# Revit family: Führungsklammer-Set, Typ B (I-III)
name_source: partatom
category: HLS-Bauteile
revit_build: Autodesk Revit 2018 (Build: 20190510_1515(x64)
units: mm (PartAtom-declared; Revit-internal decimal feet)

## family parameters
Arbeitsebenenbasiert = Ja
Beim Laden mit Abzugskörper schneiden = Nein
Bemaßung runder Anschluss = Durchmesser verwenden
Gemeinsam genutzt = Ja
Immer vertikal = Nein
Raumberechnungspunkt = Nein
Teiletyp = Normal

## types (3) — shared parameters
Fabrikat = MEFA
Firma = MEFA Befestigungs- und Montagesysteme GmbH
Material = Stahl
Materialname = S235
Mengeneinheit = St
Oberflaeche = feuerstückverzinkt
Vorgabe-Ansicht = 1219 mm
max. zul. Schublast = 4.00 kN
vpe = 1 St

## per-type parameters (varying)
| type | Artikelnummer | Faktor1 | Gewicht | Gewicht pro Bauteil | Gewindestangentyp | Klemmweite | Klemmweite Flansch max. | Klemmweite Flansch min. | Kurztext1 | Kurztext2 | Typ | min. Klemmdicke |
| Loslager ohne Abhebesicherung, Typ B III | 14711003 | 115 mm  [stored 0.377297 ft] | 1.63 kg | 1.63 kg | M12 x 310 | HEA 200, HEB180-200, IPE360-400 | 200 mm  [stored 0.656168 ft] | 170 mm  [stored 0.557743 ft] | Loslager ohne Abhebesicherung | Typ B III Klemmdicke 10 - 15 mm | B III | 10 mm |
| Loslager ohne Abhebesicherung, Typ B II | 14711002 | 85 mm  [stored 0.278871 ft] | 1.57 kg | 1.57 kg | M12 x 270 | HEA160-180, HEB140-160, IPE270-330 | 180 mm  [stored 0.590551 ft] | 160 mm  [stored 0.524934 ft] | Losölager ohne Abhebesicherung | Typ B II Klemmdicke 9 - 13 mm | B II | 9 mm |
| Loslager ohne Abhebesicherung, Typ B I | 14711001 | 5 mm  [stored 0.0164042 ft] | 1.50 kg | 1.50 kg | M12 x 220 | HEA 100-140, HEB100-120, IPE200-240 | 140 mm  [stored 0.459318 ft] | 100 mm  [stored 0.328084 ft] | Loslager ohne Abhebesiherung | Typ B I Klemmdicke 8 - 11 mm | B I | 5.2 mm |

note: [stored X ft] marks values corroborated as IEEE doubles in the binary element streams (Revit-internal decimal feet)

## geometry (parser evidence)
native form markers: Sweep x1
no freeform markers — native parametric forms only
